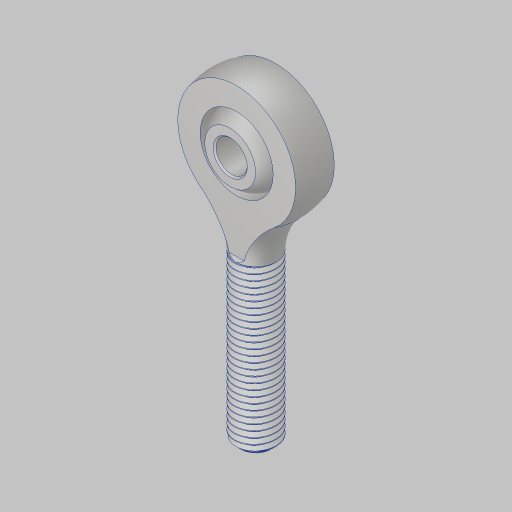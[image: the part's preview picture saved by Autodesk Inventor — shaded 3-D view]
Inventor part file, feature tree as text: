
AUTODESK INVENTOR PART (.ipt)
format: ipt  version: 2023.5 (Build 275446000, 446)  size: 679,936 bytes
history: native  units: in
note: dims shown in document units (in); Inventor stores cm internally (conversion verified against a paired STEP export)
features: chamfer x1, boolean_combine x1
ambient origin geometry x8: Origin, YZ Plane, XZ Plane, XY Plane, X Axis, Y Axis, Z Axis, Center Point
bodies: Solid1 (feature_tree), Solid2 (feature_tree)
feature tree (2):
  chamfer  "Chamfer2"  [1 undecoded]
  boolean_combine  "Combine1"
note: 1 required parameter value undecoded (feature->parameter linkage not recoverable at this tier; creation-order binding heuristic only, values carry confidence <= 0.55)
